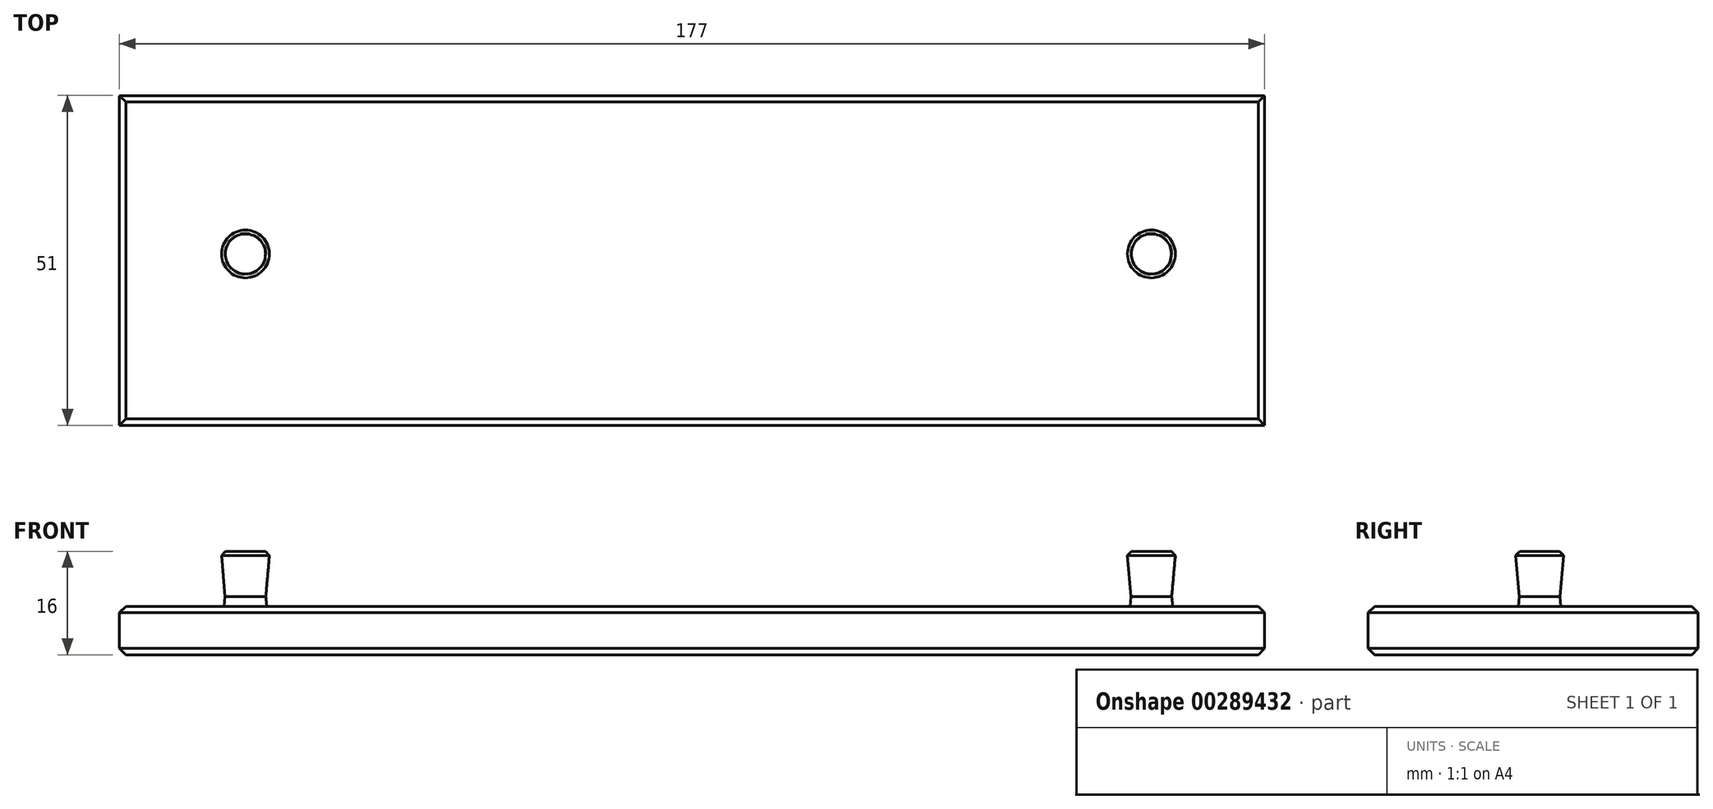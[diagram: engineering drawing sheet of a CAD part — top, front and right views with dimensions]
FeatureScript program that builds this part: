
annotation { "Feature Type Name" : "Feature", "Feature Type Description" : "" }
export const myFeature = defineFeature(function(context is Context, id is Id, definition is map)
    precondition{}
    {
        {
            var Q0;
            Q0=qCreatedBy(makeId("Top.planeOp"),FACE);
            var sketch = newSketch(context, id + "F0", { "sketchPlane" : qUnion([Q0])});
            skLineSegment(sketch, "E0.bottom", {"start": v(-110.02, 4.55) * mm, "end": v(66.98, 4.55) * mm});
            skLineSegment(sketch, "E0.top", {"start": v(-110.02, -46.45) * mm, "end": v(66.98, -46.45) * mm});
            skLineSegment(sketch, "E0.left", {"start": v(-110.02, 4.55) * mm, "end": v(-110.02, -46.45) * mm});
            skLineSegment(sketch, "E0.right", {"start": v(66.98, 4.55) * mm, "end": v(66.98, -46.45) * mm});
            skPoint(sketch, "E1", {"position": v(-90.52, -19.95) * mm});
            skPoint(sketch, "E2", {"position": v(49.48, -19.95) * mm});
            skCircle(sketch, "E3", {"center": v(-90.52, -19.95) * mm, "radius": 3.3 * mm});
            skCircle(sketch, "E4", {"center": v(49.48, -19.95) * mm, "radius": 3.3 * mm});
            skSolve(sketch);
        }
        {
            var Q0;
            Q0 = qSketchRegion(id + "F0", true);
            var Q1;
            Q1=makeQuery(id+"F0.imprint","IMPRINT",FACE,{"disambiguationData":[TD([[makeQuery(id+"F0.imprint","IMPRINT",EDGE,{"derivedFrom":sQuery(id+"F0.wireOp",EDGE,"E3")}),1.0]])]});
            var Q2;
            Q2=makeQuery(id+"F0.imprint","IMPRINT",FACE,{"disambiguationData":[TD([[makeQuery(id+"F0.imprint","IMPRINT",EDGE,{"derivedFrom":sQuery(id+"F0.wireOp",EDGE,"E4")}),1.0]])]});
            extrude(context, id + "F1", {"entities" : qUnion([Q0, Q1, Q2]), "oppositeDirection" : true, "depth" : 7.5 * mm});
        }
        {
            var Q0;
            Q0=makeQuery(id+"F0.imprint","IMPRINT",FACE,{"disambiguationData":[TD([[makeQuery(id+"F0.imprint","IMPRINT",EDGE,{"derivedFrom":sQuery(id+"F0.wireOp",EDGE,"E3")}),1.0]])]});
            var Q1;
            Q1=makeQuery(id+"F0.imprint","IMPRINT",FACE,{"disambiguationData":[TD([[makeQuery(id+"F0.imprint","IMPRINT",EDGE,{"derivedFrom":sQuery(id+"F0.wireOp",EDGE,"E4")}),1.0]])]});
            extrude(context, id + "F2", {"entities" : qUnion([Q0, Q1]), "operationType" : NewBodyOperationType.ADD, "depth" : 1.5 * mm, "hasDraft" : true, "draftAngle" : 6 * degree, "draftPullDirection" : true});
        }
        {
            var Q0;
            Q0=makeQuery(id+"F2.opExtrude","CAP_FACE",FACE,{"disambiguationData":[OSD([sQuery(id+"F0.wireOp",EDGE,"E4")])],"isStart":false});
            var Q1;
            Q1=makeQuery(id+"F2.opExtrude","CAP_FACE",FACE,{"disambiguationData":[OSD([sQuery(id+"F0.wireOp",EDGE,"E3")])],"isStart":false});
            extrude(context, id + "F3", {"entities" : qUnion([Q0, Q1]), "operationType" : NewBodyOperationType.ADD, "depth" : 7 * mm, "hasDraft" : true, "draftAngle" : 5 * degree});
        }
        {
            var Q0;
            Q0=makeQuery(id+"F3.opExtrude","CAP_EDGE",EDGE,{"disambiguationData":[OSD([sQuery(id+"F0.wireOp",EDGE,"E3")])],"isStart":false});
            var Q1;
            Q1=makeQuery(id+"F3.opExtrude","CAP_EDGE",EDGE,{"disambiguationData":[OSD([sQuery(id+"F0.wireOp",EDGE,"E4")])],"isStart":false});
            chamfer(context, id + "F4", {"entities" : qUnion([Q0, Q1]), "width" : 0.6 * mm, "tangentPropagation" : true});
        }
        {
            var Q0;
            Q0=makeQuery(id+"F1.opExtrude","CAP_EDGE",EDGE,{"disambiguationData":[OSD([sQuery(id+"F0.wireOp",EDGE,"E0.left")])],"isStart":true});
            var Q1;
            Q1=makeQuery(id+"F1.opExtrude","CAP_EDGE",EDGE,{"disambiguationData":[OSD([sQuery(id+"F0.wireOp",EDGE,"E0.bottom")])],"isStart":true});
            var Q2;
            Q2=makeQuery(id+"F1.opExtrude","CAP_EDGE",EDGE,{"disambiguationData":[OSD([sQuery(id+"F0.wireOp",EDGE,"E0.top")])],"isStart":true});
            var Q3;
            Q3=makeQuery(id+"F1.opExtrude","CAP_EDGE",EDGE,{"disambiguationData":[OSD([sQuery(id+"F0.wireOp",EDGE,"E0.right")])],"isStart":true});
            var Q4;
            Q4=makeQuery(id+"F1.opExtrude","CAP_FACE",FACE,{"disambiguationData":[OSD([sQuery(id+"F0.wireOp",EDGE,"E0.bottom"),sQuery(id+"F0.wireOp",EDGE,"E0.top"),sQuery(id+"F0.wireOp",EDGE,"E0.left"),sQuery(id+"F0.wireOp",EDGE,"E0.right")])],"isStart":false});
            chamfer(context, id + "F5", {"entities" : qUnion([Q0, Q1, Q2, Q3, Q4]), "width" : 1 * mm, "tangentPropagation" : true});
        }
    });
